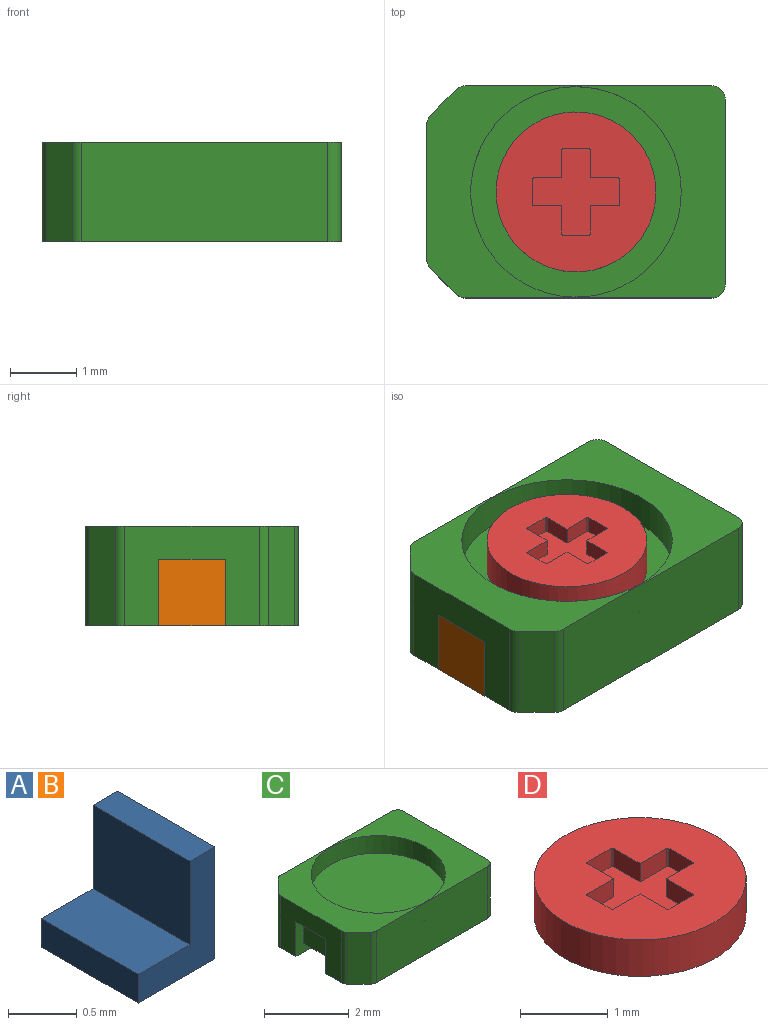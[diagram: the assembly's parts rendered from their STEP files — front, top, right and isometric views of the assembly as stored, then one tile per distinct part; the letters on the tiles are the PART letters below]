
ASSEMBLY  parts=4 mates=9
PART A: 8 faces, bbox 0.8x1x1 mm
  f0: plane 1x0.75mm, normal (-1,0,0), area 0.7mm2, adj f1,f3,f4,f6
  f1: plane 1x0.79mm, normal (0,-1,0), area 0.4mm2, adj f0,f2,f4,f5,f6,f7
  f2: plane 1x0.79mm, normal (0,0,-1), area 0.8mm2, adj f1,f3,f5,f7
  f3: plane 1x0.79mm, normal (0,1,0), area 0.4mm2, adj f0,f2,f4,f5,f6,f7
  f4: plane 1x0.25mm, normal (0,0,1), area 0.3mm2, adj f0,f1,f3,f5
  f5: plane 1x1mm, normal (1,0,0), area 1mm2, adj f1,f2,f3,f4
  f6: plane 1x0.53mm, normal (0,0,1), area 0.5mm2, adj f0,f1,f3,f7
  f7: plane 1x0.25mm, normal (-1,0,0), area 0.3mm2, adj f1,f2,f3,f6
PART B: same geometry as A
PART C: 28 faces, bbox 4.5x3.2x1.5 mm
  f0: plane 1x0.75mm, normal (-1,0,0), area 0.7mm2, adj f15,f16,f17,f25
  f1: plane 4.5x3.2mm, normal (0,0,-1), area 12.6mm2, adj f2,f3,f4,f5,f6,f7,f8,f9
  f2: plane 1.5x0.38mm, normal (-0.71,-0.71,0), area 0.8mm2, adj f1,f3,f13,f14
  f3: cylinder r=0.2mm len=1.5mm, axis (0,0,-1), area 0.2mm2, adj f1,f2,f4,f14
  f4: plane 3.72x1.5mm, normal (0,-1,0), area 5.6mm2, adj f1,f3,f5,f14
  f5: cylinder r=0.2mm len=1.5mm, axis (0,0,-1), area 0.5mm2, adj f1,f4,f6,f14
  f6: plane 2.8x1.5mm, normal (1,0,0), area 3.2mm2, adj f1,f5,f7,f14,f18,f19,f20
  f7: cylinder r=0.2mm len=1.5mm, axis (0,0,-1), area 0.5mm2, adj f1,f6,f8,f14
  f8: plane 3.72x1.5mm, normal (0,1,0), area 5.6mm2, adj f1,f7,f9,f14
  f9: cylinder r=0.2mm len=1.5mm, axis (0,0,-1), area 0.2mm2, adj f1,f8,f10,f14
  f10: plane 1.5x0.38mm, normal (-0.71,0.71,0), area 0.8mm2, adj f1,f9,f11,f14
  f11: cylinder r=0.2mm len=1.5mm, axis (0,0,-1), area 0.2mm2, adj f1,f10,f12,f14
  f12: plane 2.04x1.5mm, normal (-1,0,0), area 2.1mm2, adj f1,f11,f13,f14,f15,f16,f17
  f13: cylinder r=0.2mm len=1.5mm, axis (0,0,-1), area 0.2mm2, adj f1,f2,f12,f14
  f14: plane 4.5x3.2mm, normal (0,0,1), area 6.2mm2, adj f2,f3,f4,f5,f6,f7,f8,f9
  f15: plane 1x0.79mm, normal (0,-1,0), area 0.4mm2, adj f0,f1,f12,f17,f24,f25
  f16: plane 1x0.79mm, normal (0,1,0), area 0.4mm2, adj f0,f1,f12,f17,f24,f25
  f17: plane 1x0.25mm, normal (0,0,-1), area 0.3mm2, adj f0,f12,f15,f16
  f18: plane 1x0.79mm, normal (0,-1,0), area 0.4mm2, adj f1,f6,f19,f21,f22,f23
  f19: plane 1x0.25mm, normal (0,0,-1), area 0.3mm2, adj f6,f18,f20,f21
  f20: plane 1x0.79mm, normal (0,1,0), area 0.4mm2, adj f1,f6,f19,f21,f22,f23
  f21: plane 1x0.75mm, normal (1,0,0), area 0.7mm2, adj f18,f19,f20,f23
  f22: plane 1x0.25mm, normal (1,0,0), area 0.3mm2, adj f1,f18,f20,f23
  f23: plane 1x0.53mm, normal (0,0,-1), area 0.5mm2, adj f18,f20,f21,f22
  f24: plane 1x0.25mm, normal (-1,0,0), area 0.3mm2, adj f1,f15,f16,f25
  f25: plane 1x0.53mm, normal (0,0,-1), area 0.5mm2, adj f0,f15,f16,f24
  f26: cylinder r=1.59mm len=3.18mm, axis (0,0,1), area 5.1mm2, adj f14,f27
  f27: plane 3.18x3.18mm, normal (0,0,1), area 7.9mm2, adj f26
PART D: 24 faces, bbox 2.4x2.4x0.5 mm
  f0: plane 2.41x2.41mm, normal (0,0,-1), area 4.6mm2, adj f2
  f1: plane 2.41x2.41mm, normal (0,0,1), area 3.6mm2, adj f2,f3,f4,f5,f6,f7,f8,f9
  f2: cylinder r=1.21mm len=2.41mm, axis (0,0,1), area 3.9mm2, adj f0,f1
  f3: plane 0.42x0.25mm, normal (-1,0,0), area 0.1mm2, adj f1,f4,f22,f23
  f4: plane 0.42x0.25mm, normal (0,1,0), area 0.1mm2, adj f1,f3,f5,f23
  f5: cylinder r=0.02mm len=0.25mm, axis (0,0,1), area 0mm2, adj f1,f4,f6,f23
  f6: plane 0.38x0.25mm, normal (-1,0,0), area 0.1mm2, adj f1,f5,f7,f23
  f7: cylinder r=0.02mm len=0.25mm, axis (0,0,1), area 0mm2, adj f1,f6,f8,f23
  f8: plane 0.42x0.25mm, normal (0,-1,0), area 0.1mm2, adj f1,f7,f9,f23
  f9: plane 0.42x0.25mm, normal (-1,0,0), area 0.1mm2, adj f1,f8,f10,f23
  f10: cylinder r=0.02mm len=0.25mm, axis (0,0,1), area 0mm2, adj f1,f9,f11,f23
  f11: plane 0.38x0.25mm, normal (0,-1,0), area 0.1mm2, adj f1,f10,f12,f23
  f12: cylinder r=0.02mm len=0.25mm, axis (0,0,1), area 0mm2, adj f1,f11,f13,f23
  f13: plane 0.42x0.25mm, normal (1,0,0), area 0.1mm2, adj f1,f12,f14,f23
  f14: plane 0.42x0.25mm, normal (0,-1,0), area 0.1mm2, adj f1,f13,f15,f23
  f15: cylinder r=0.02mm len=0.25mm, axis (0,0,1), area 0mm2, adj f1,f14,f16,f23
  f16: plane 0.38x0.25mm, normal (1,0,0), area 0.1mm2, adj f1,f15,f17,f23
  f17: cylinder r=0.02mm len=0.25mm, axis (0,0,1), area 0mm2, adj f1,f16,f18,f23
  f18: plane 0.42x0.25mm, normal (0,1,0), area 0.1mm2, adj f1,f17,f19,f23
  f19: plane 0.42x0.25mm, normal (1,0,0), area 0.1mm2, adj f1,f18,f20,f23
  f20: cylinder r=0.02mm len=0.25mm, axis (0,0,1), area 0mm2, adj f1,f19,f21,f23
  f21: plane 0.38x0.25mm, normal (0,1,0), area 0.1mm2, adj f1,f20,f22,f23
  f22: cylinder r=0.02mm len=0.25mm, axis (0,0,1), area 0mm2, adj f1,f3,f21,f23
  f23: plane 1.31x1.31mm, normal (0,0,1), area 0.9mm2, adj f3,f4,f5,f6,f7,f8,f9,f10
PLACE A rot(axis=(0,0,-1),0deg) t=(0,0,0)mm
PLACE B rot(axis=(0,0,-1),180deg) t=(0,0,0)mm
PLACE C rot(axis=(0,0,1),0deg) t=(0,0,0)mm
PLACE D rot(axis=(0,0,1),0deg) t=(0,0,1.95)mm
MATE planar A.f0 <-> C.f21  axis (-1,0,0) through (2,0,0.63)mm
MATE planar B.f3 <-> C.f16  axis (0,-1,0) through (-2,-0.5,0.25)mm
MATE planar C.f23 <-> A.f6  axis (0,0,-1) through (1.73,0,0.25)mm
MATE cylindrical C.f26 <-> D.f2  axis (0,0,1) through (0,0,1.25)mm
MATE planar D.f2 <-> C.f26  axis (0,0,-1) through (0,0,0.99)mm
MATE parallel D.f18 <-> C.f4  axis (0,1,0) through (-0.21,-0.21,1.37)mm
MATE planar B.f7 <-> C.f24  axis (1,0,0) through (-1.46,0,0.13)mm
MATE planar A.f1 <-> C.f20  axis (0,-1,0) through (2,-0.5,0.25)mm
MATE planar B.f6 <-> C.f25  axis (0,0,1) through (-1.73,0,0.25)mm
